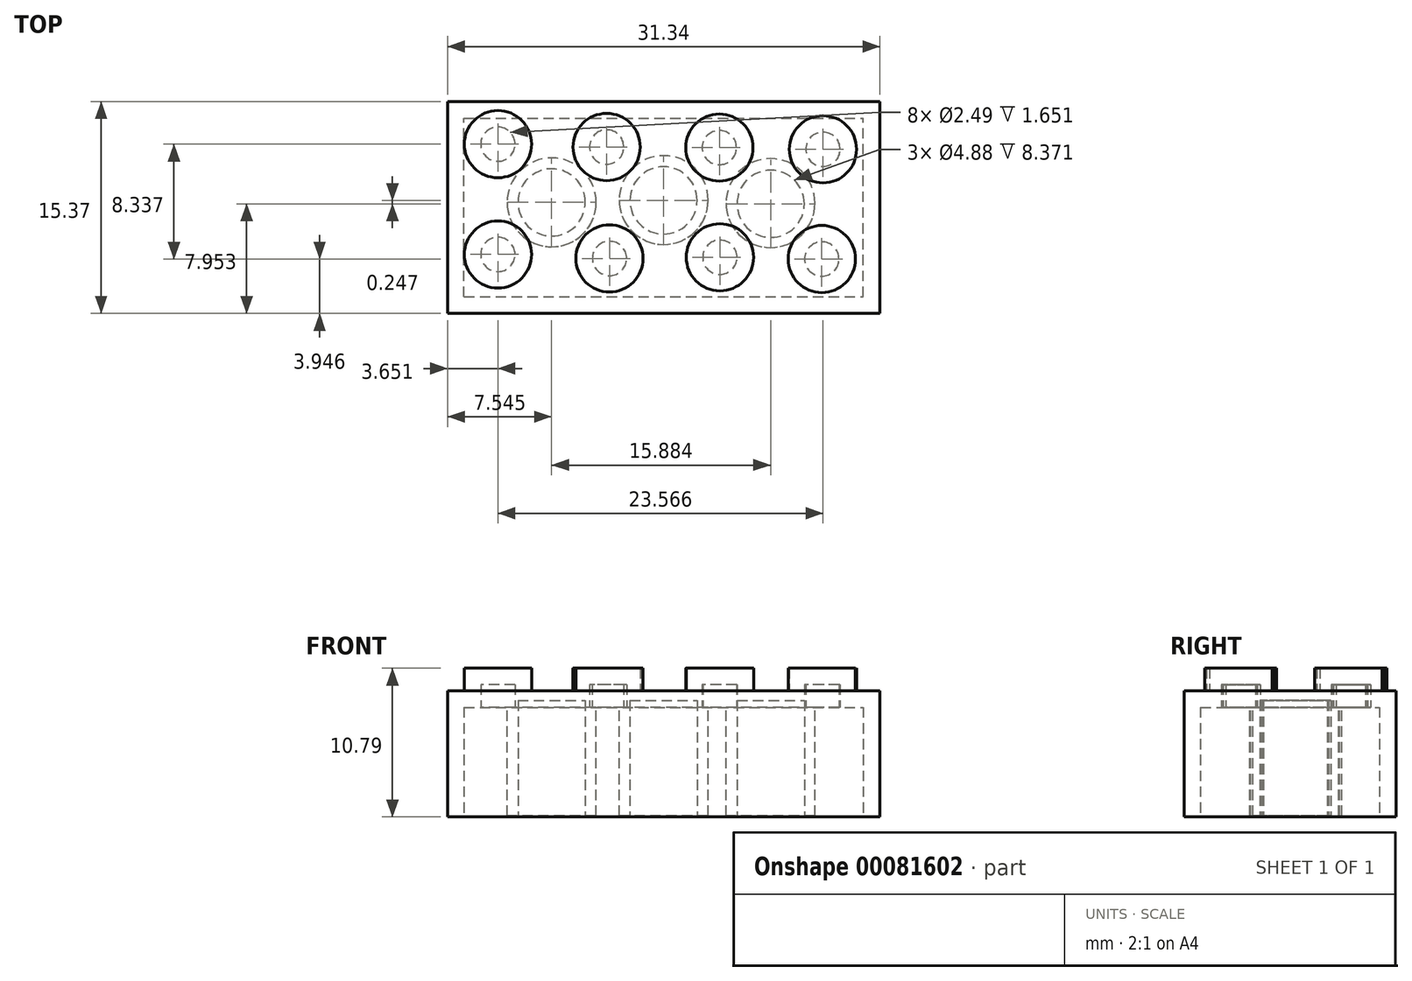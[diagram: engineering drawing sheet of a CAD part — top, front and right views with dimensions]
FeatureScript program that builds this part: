
annotation { "Feature Type Name" : "Feature", "Feature Type Description" : "" }
export const myFeature = defineFeature(function(context is Context, id is Id, definition is map)
    precondition{}
    {
        {
            var Q0;
            Q0=qCreatedBy(makeId("Front.planeOp"),FACE);
            var sketch = newSketch(context, id + "F0", { "sketchPlane" : qUnion([Q0])});
            skLineSegment(sketch, "E0.bottom", {"start": v(-15.67, 4.57) * mm, "end": v(15.67, 4.57) * mm});
            skLineSegment(sketch, "E0.top", {"start": v(-15.67, -4.57) * mm, "end": v(15.67, -4.57) * mm});
            skLineSegment(sketch, "E0.left", {"start": v(-15.67, 4.57) * mm, "end": v(-15.67, -4.57) * mm});
            skLineSegment(sketch, "E0.right", {"start": v(15.67, 4.57) * mm, "end": v(15.67, -4.57) * mm});
            skPoint(sketch, "E0.middle", {"position": v(0, 0) * mm});
            skSolve(sketch);
        }
        {
            var Q0;
            Q0=makeQuery(id+"F0.imprint","IMPRINT",FACE,{"disambiguationData":[TD([[makeQuery(id+"F0.imprint","IMPRINT",EDGE,{"derivedFrom":sQuery(id+"F0.wireOp",EDGE,"E0.bottom")}),-1.0]])]});
            extrude(context, id + "F1", {"entities" : qUnion([Q0]), "depth" : 15.37 * mm});
        }
        {
            var Q0;
            Q0=makeQuery(id+"F1.opExtrude","SWEPT_FACE",FACE,{"disambiguationData":[OSD([sQuery(id+"F0.wireOp",EDGE,"E0.bottom")])]});
            var sketch = newSketch(context, id + "F2", { "sketchPlane" : qUnion([Q0])});
            skCircle(sketch, "E1", {"center": v(-12.02, -3.09) * mm, "radius": 2.44 * mm});
            skCircle(sketch, "E2", {"center": v(-4.14, -3.3) * mm, "radius": 2.44 * mm});
            skCircle(sketch, "E3", {"center": v(4.04, -3.33) * mm, "radius": 2.44 * mm});
            skCircle(sketch, "E4", {"center": v(11.55, -3.46) * mm, "radius": 2.44 * mm});
            skCircle(sketch, "E5", {"center": v(-12.02, -11.1) * mm, "radius": 2.44 * mm});
            skCircle(sketch, "E6", {"center": v(-3.93, -11.38) * mm, "radius": 2.44 * mm});
            skCircle(sketch, "E7", {"center": v(4.08, -11.3) * mm, "radius": 2.44 * mm});
            skCircle(sketch, "E8", {"center": v(11.46, -11.42) * mm, "radius": 2.44 * mm});
            skSolve(sketch);
        }
        {
            var Q0;
            Q0=makeQuery(id+"F2.imprint","IMPRINT",FACE,{"disambiguationData":[TD([[makeQuery(id+"F2.imprint","IMPRINT",EDGE,{"derivedFrom":sQuery(id+"F2.wireOp",EDGE,"E1")}),1.0]])]});
            var Q1;
            Q1=makeQuery(id+"F2.imprint","IMPRINT",FACE,{"disambiguationData":[TD([[makeQuery(id+"F2.imprint","IMPRINT",EDGE,{"derivedFrom":sQuery(id+"F2.wireOp",EDGE,"E2")}),1.0]])]});
            var Q2;
            Q2=makeQuery(id+"F2.imprint","IMPRINT",FACE,{"disambiguationData":[TD([[makeQuery(id+"F2.imprint","IMPRINT",EDGE,{"derivedFrom":sQuery(id+"F2.wireOp",EDGE,"E3")}),1.0]])]});
            var Q3;
            Q3=makeQuery(id+"F2.imprint","IMPRINT",FACE,{"disambiguationData":[TD([[makeQuery(id+"F2.imprint","IMPRINT",EDGE,{"derivedFrom":sQuery(id+"F2.wireOp",EDGE,"E4")}),1.0]])]});
            var Q4;
            Q4=makeQuery(id+"F2.imprint","IMPRINT",FACE,{"disambiguationData":[TD([[makeQuery(id+"F2.imprint","IMPRINT",EDGE,{"derivedFrom":sQuery(id+"F2.wireOp",EDGE,"E8")}),1.0]])]});
            var Q5;
            Q5=makeQuery(id+"F2.imprint","IMPRINT",FACE,{"disambiguationData":[TD([[makeQuery(id+"F2.imprint","IMPRINT",EDGE,{"derivedFrom":sQuery(id+"F2.wireOp",EDGE,"E7")}),1.0]])]});
            var Q6;
            Q6=makeQuery(id+"F2.imprint","IMPRINT",FACE,{"disambiguationData":[TD([[makeQuery(id+"F2.imprint","IMPRINT",EDGE,{"derivedFrom":sQuery(id+"F2.wireOp",EDGE,"E6")}),1.0]])]});
            var Q7;
            Q7=makeQuery(id+"F2.imprint","IMPRINT",FACE,{"disambiguationData":[TD([[makeQuery(id+"F2.imprint","IMPRINT",EDGE,{"derivedFrom":sQuery(id+"F2.wireOp",EDGE,"E5")}),1.0]])]});
            var Q8;
            Q8=sQuery(id+"F2.wireOp",EDGE,"E1");
            var Q9;
            Q9=sQuery(id+"F2.wireOp",EDGE,"E5");
            var Q10;
            Q10=sQuery(id+"F2.wireOp",EDGE,"E2");
            var Q11;
            Q11=sQuery(id+"F2.wireOp",EDGE,"E6");
            var Q12;
            Q12=sQuery(id+"F2.wireOp",EDGE,"E7");
            var Q13;
            Q13=sQuery(id+"F2.wireOp",EDGE,"E3");
            var Q14;
            Q14=sQuery(id+"F2.wireOp",EDGE,"E4");
            var Q15;
            Q15=sQuery(id+"F2.wireOp",EDGE,"E8");
            extrude(context, id + "F3", {"entities" : qUnion([Q0, Q1, Q2, Q3, Q4, Q5, Q6, Q7]), "operationType" : NewBodyOperationType.ADD, "surfaceEntities" : qUnion([Q8, Q9, Q10, Q11, Q12, Q13, Q14, Q15]), "depth" : 1.65 * mm});
        }
        {
            var Q0;
            Q0=makeQuery(id+"F1.opExtrude","SWEPT_FACE",FACE,{"disambiguationData":[OSD([sQuery(id+"F0.wireOp",EDGE,"E0.top")])]});
            shell(context, id + "F4", {"entities" : qUnion([Q0]), "thickness" : 1.2 * mm});
        }
        {
            var Q0;
            Q0=makeQuery(id+"F4.opShell","OFFSET_FACE",FACE,{"disambiguationData":[OSD([sQuery(id+"F0.wireOp",EDGE,"E0.bottom")])]});
            var sketch = newSketch(context, id + "F5", { "sketchPlane" : qUnion([Q0])});
            skCircle(sketch, "E9", {"center": v(0, 7.15) * mm, "radius": 3.23 * mm});
            skCircle(sketch, "E10", {"center": v(7.74, 7.37) * mm, "radius": 3.23 * mm});
            skCircle(sketch, "E11", {"center": v(-8.13, 7.31) * mm, "radius": 3.23 * mm});
            skSolve(sketch);
        }
        {
            var Q0;
            Q0=makeQuery(id+"F5.imprint","IMPRINT",FACE,{"disambiguationData":[TD([[makeQuery(id+"F5.imprint","IMPRINT",EDGE,{"derivedFrom":sQuery(id+"F5.wireOp",EDGE,"E11")}),1.0]])]});
            var Q1;
            Q1=makeQuery(id+"F5.imprint","IMPRINT",FACE,{"disambiguationData":[TD([[makeQuery(id+"F5.imprint","IMPRINT",EDGE,{"derivedFrom":sQuery(id+"F5.wireOp",EDGE,"E9")}),1.0]])]});
            var Q2;
            Q2=makeQuery(id+"F5.imprint","IMPRINT",FACE,{"disambiguationData":[TD([[makeQuery(id+"F5.imprint","IMPRINT",EDGE,{"derivedFrom":sQuery(id+"F5.wireOp",EDGE,"E10")}),1.0]])]});
            extrude(context, id + "F6", {"entities" : qUnion([Q0, Q1, Q2]), "operationType" : NewBodyOperationType.ADD, "depth" : 7.88 * mm});
        }
        {
            var Q0;
            Q0=makeQuery(id+"F6.opExtrude","CAP_FACE",FACE,{"disambiguationData":[OSD([sQuery(id+"F5.wireOp",EDGE,"E11")])],"isStart":false});
            var sketch = newSketch(context, id + "F7", { "sketchPlane" : qUnion([Q0])});
            skCircle(sketch, "E12", {"center": v(-8.13, 7.31) * mm, "radius": 2.44 * mm});
            skCircle(sketch, "E13", {"center": v(-0.01, 7.17) * mm, "radius": 2.44 * mm});
            skCircle(sketch, "E14", {"center": v(7.76, 7.42) * mm, "radius": 2.44 * mm});
            skSolve(sketch);
        }
        {
            var Q0;
            Q0=makeQuery(id+"F7.imprint","IMPRINT",FACE,{"disambiguationData":[TD([[makeQuery(id+"F7.imprint","IMPRINT",EDGE,{"derivedFrom":sQuery(id+"F7.wireOp",EDGE,"E12")}),1.0]])]});
            var Q1;
            Q1=makeQuery(id+"F7.imprint","IMPRINT",FACE,{"disambiguationData":[TD([[makeQuery(id+"F7.imprint","IMPRINT",EDGE,{"derivedFrom":sQuery(id+"F7.wireOp",EDGE,"E13")}),1.0]])]});
            var Q2;
            Q2=makeQuery(id+"F7.imprint","IMPRINT",FACE,{"disambiguationData":[TD([[makeQuery(id+"F7.imprint","IMPRINT",EDGE,{"derivedFrom":sQuery(id+"F7.wireOp",EDGE,"E14")}),1.0]])]});
            extrude(context, id + "F8", {"entities" : qUnion([Q0, Q1, Q2]), "operationType" : NewBodyOperationType.REMOVE, "oppositeDirection" : true, "depth" : 8.37 * mm});
        }
        {
            var Q0;
            Q0=makeQuery(id+"F4.opShell","OFFSET_FACE",FACE,{"disambiguationData":[OSD([sQuery(id+"F0.wireOp",EDGE,"E0.bottom")])]});
            var sketch = newSketch(context, id + "F9", { "sketchPlane" : qUnion([Q0])});
            skLineSegment(sketch, "E15", {"start": v(0, 14.17) * mm, "end": v(0, 10.37) * mm});
            skPoint(sketch, "E15.endSnap0", {"position": v(0, 1.2) * mm});
            skLineSegment(sketch, "E16", {"start": v(0, 3.92) * mm, "end": v(0, 1.2) * mm});
            skSolve(sketch);
        }
        {
            var Q0;
            Q0=sQuery(id+"F9.wireOp",EDGE,"E15");
            var Q1;
            Q1=sQuery(id+"F9.wireOp",EDGE,"E16");
            extrude(context, id + "F10", {"bodyType" : ToolBodyType.SURFACE, "surfaceEntities" : qUnion([Q0, Q1]), "depth" : 6.5 * mm});
        }
    });
